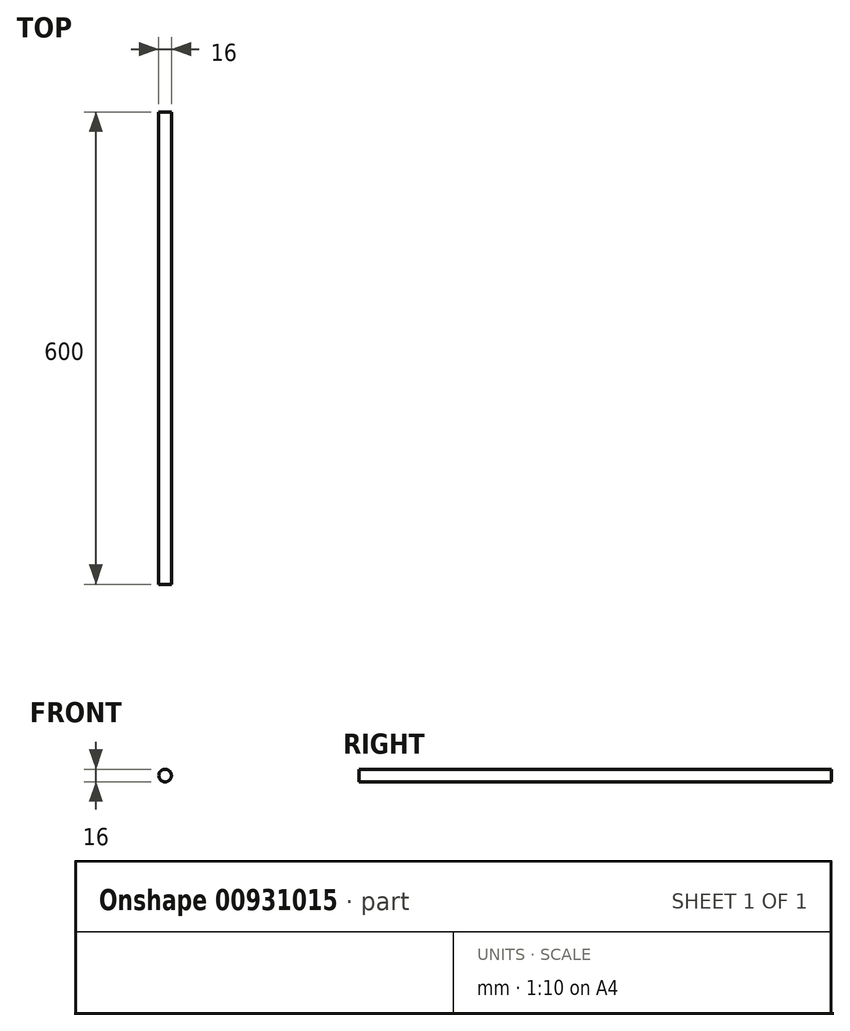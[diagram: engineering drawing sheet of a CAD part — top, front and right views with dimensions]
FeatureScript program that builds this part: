
annotation { "Feature Type Name" : "Feature", "Feature Type Description" : "" }
export const myFeature = defineFeature(function(context is Context, id is Id, definition is map)
    precondition{}
    {
        {
            var Q0;
            Q0=qCreatedBy(makeId("Front.planeOp"),FACE);
            var sketch = newSketch(context, id + "F0", { "sketchPlane" : qUnion([Q0])});
            skCircle(sketch, "E0", {"center": v(0, 0) * mm, "radius": 8 * mm});
            skSolve(sketch);
        }
        {
            var Q0;
            Q0=qSketchRegion(id+"F0",true);
            extrude(context, id + "F1", {"entities" : qUnion([Q0]), "oppositeDirection" : true, "depth" : 600 * mm, "offsetDistance" : 25 * mm});
        }
    });
